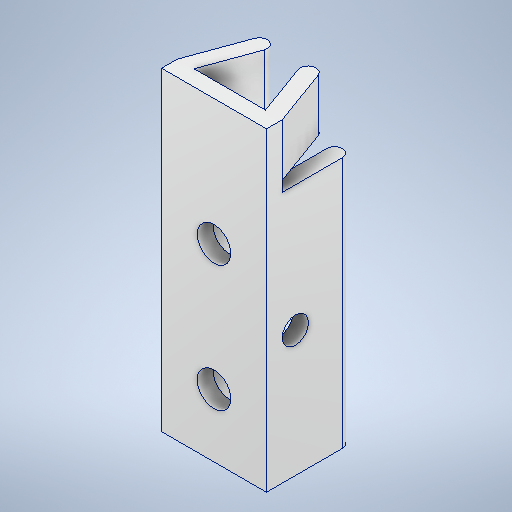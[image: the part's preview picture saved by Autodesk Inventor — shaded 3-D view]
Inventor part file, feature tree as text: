
AUTODESK INVENTOR PART (.ipt)
format: ipt  version: 2025 (Build 290162000, 162)  size: 342,528 bytes
history: native  units: mm
features: sketch x5, projected_geometry x4, extrude x3, hole x2, other x1, fillet x1
ambient origin geometry x8: Origin, YZ Plane, XZ Plane, XY Plane, X Axis, Y Axis, Z Axis, Center Point
bodies: Body1 (feature_tree)
feature tree (16):
  other  "Těleso1"
  extrude  "Vysunutí1"  Depth=10.0mm
  extrude  "Vysunutí2"  Depth=8.0mm
  extrude  "Vysunutí3"  Depth=1.5mm
  fillet  "Zaoblení1"  Radius=1.5mm
  hole  "Díra1"  [1 undecoded]
  hole  "Díra2"  [1 undecoded]
  sketch  "Náčrt1"
  sketch  "Náčrt2"
  projected_geometry  "Promítnutá smyčka1"
  sketch  "Náčrt3"
  projected_geometry  "Promítnutá smyčka2"
  sketch  "Náčrt4"
  projected_geometry  "Promítnutá smyčka3"
  sketch  "Náčrt5"
  projected_geometry  "Promítnutá smyčka4"
note: 2 required parameter values undecoded (feature->parameter linkage not recoverable at this tier; creation-order binding heuristic only, values carry confidence <= 0.55)
